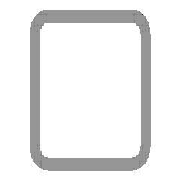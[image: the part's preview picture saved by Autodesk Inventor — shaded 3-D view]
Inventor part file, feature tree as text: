
AUTODESK INVENTOR PART (.ipt)
format: ipt  version: 2022 (Build 260153000, 153)  size: 139,264 bytes
history: native  units: mm (DEFAULTED — no unit token found)
features: other x4, sketch x3, plane x1
ambient origin geometry x8: Origin, YZ Plane, XZ Plane, XY Plane, X Axis, Y Axis, Z Axis, Center Point
bodies: Solid1 (feature_tree), Body (feature_tree)
feature tree (8):
  parser-record x1  (decoder bookkeeping rows leaked as tree rows — omitted from the tree; the rows remain in map.json)
  other  "Driven Length"
  other  "Start plane"
  other  "End plane"
  sketch  "Sketch"  dims[d7=4.5mm d10=30.0mm d11=30.0mm d12=3.0mm d13=-0.0mm d14=180.0mm d15=15.0mm d16=15.0mm d17=90.0deg d18=180.0mm]
  sketch  "Sketch3"  dims[d3=180.0mm]
  plane  "Work Plane3"
  sketch  "Sketch4"  dims[d4=0.0mm]
